# Revit family: QF_COMENDA_CE90
name_source: partatom
category: Attrezzature speciali
units: mm (PartAtom-declared; Revit-internal decimal feet)

## family parameters
Basato su piano di lavoro = No
Condiviso = No
Numero OmniClass = 23.40.40.14
Punto di calcolo locali = No
Quota connettore circolare = Usa diametro
Sempre verticale = Sì
Taglio con vuoti quando caricato = No
Tipo di parte = Normale
Titolo OmniClass = Food Service Equipment

## types (3) — shared parameters
Accessorio = No
Altezza = 1495 mm
Assorbimento corrente minimo = 0 A
Cavo di allacciamento compreso nella fornitura = No
Corrente a pieno carico = 11 A
Diametro di scarico indiretto acqua = 51 mm
Diametro raccordo acqua calda = 19 mm
Fase = 3
Frequenza = 50 Hz
Lunghezza = 620 mm  [stored 2.03412 ft]
Numero dei poli = 3
Peso netto = 0.00 kg
Portata acqua calda = 0.0 L/s
Potenza apparente = 7500 VA
Potenza elettrica = 7500 W
Produttore = HOONVED
Profondità = 742 mm  [stored 2.43438 ft]
Protezione contro le sovracorrenti = 0 A
Temperatura di alimentazione acqua calda = 60 °C
Temperatura raccomandata per acqua calda  = 60 °C
Tensione = 400 V
URL = https://www.hoonved.com
zero-valued in all types: Costo

## per-type parameters (varying)
| type | Descrizione | Modello |
| H59022 | MULTIPURPOSE WASHER 500X600 MM RACK SIZE | C90E |
| H59020 | MULTIPURPOSE WASHER 500X600 MM RACK SIZE WITH BREAK TANK | C90EBT |
| H59023 | MULTIPURPOSE WASHER 500X600 MM RACK SIZE WITH WATER SOFTENER | C90DE |

note: [stored X ft] marks values corroborated as IEEE doubles in the binary element streams (Revit-internal decimal feet)

## geometry (parser evidence)
native form markers: Sweep x1
no freeform markers — native parametric forms only
